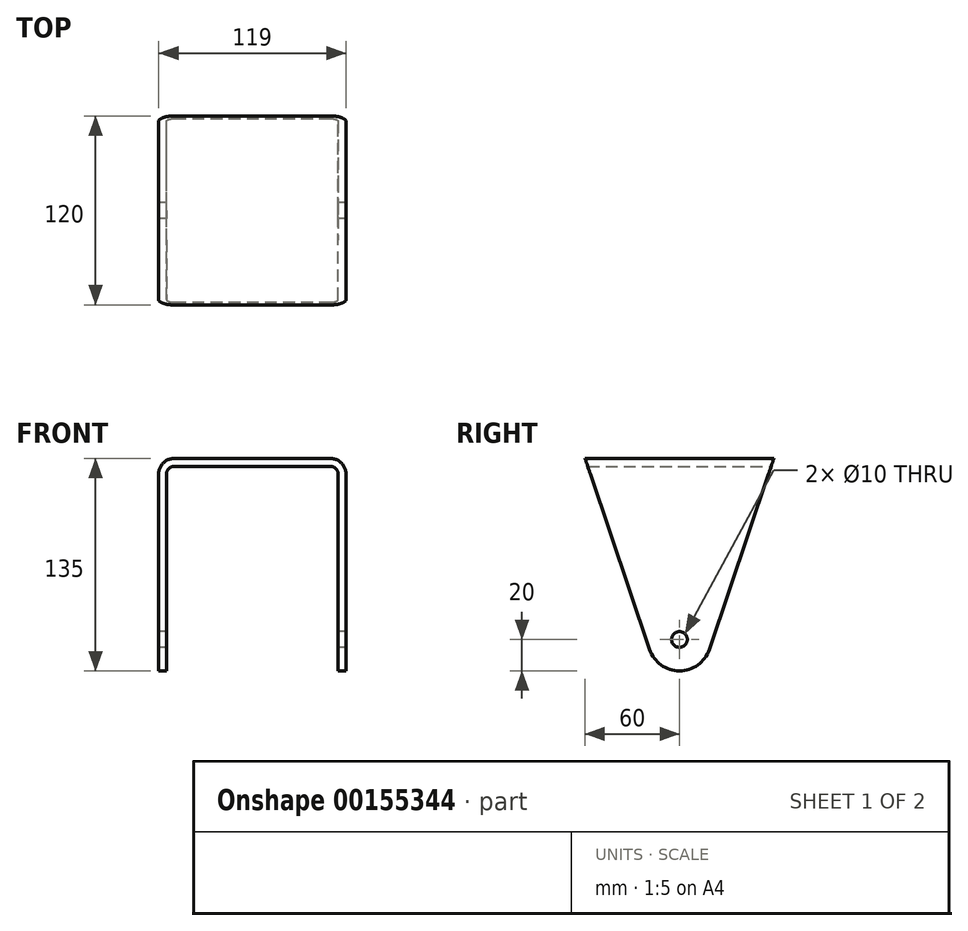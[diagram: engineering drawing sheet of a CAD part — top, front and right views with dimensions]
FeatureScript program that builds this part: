
annotation { "Feature Type Name" : "Feature", "Feature Type Description" : "" }
export const myFeature = defineFeature(function(context is Context, id is Id, definition is map)
    precondition{}
    {
        {
            var Q0;
            Q0=qCreatedBy(makeId("Front.planeOp"),FACE);
            var sketch = newSketch(context, id + "F0", { "sketchPlane" : qUnion([Q0])});
            skLineSegment(sketch, "E0", {"start": v(-29.5, 0) * mm, "end": v(-29.5, -20) * mm});
            skLineSegment(sketch, "E1", {"start": v(-29.5, -20) * mm, "end": v(-34.5, -20) * mm});
            skLineSegment(sketch, "E2", {"start": v(-34.5, -20) * mm, "end": v(-34.5, 105) * mm});
            skLineSegment(sketch, "E3", {"start": v(-24.5, 115) * mm, "end": v(25, 115) * mm});
            skLineSegment(sketch, "E4", {"start": v(-29.5, 0) * mm, "end": v(-29.5, 105) * mm});
            skLineSegment(sketch, "E5.0", {"start": v(-24.5, 110) * mm, "end": v(25, 110) * mm});
            skArc(sketch, "E6.filletArc", {"start": v(-24.5, 110) * mm, "mid": v(-28.04, 108.54) * mm, "end": v(-29.5, 105) * mm});
            skArc(sketch, "E7.0", {"start": v(-24.5, 115) * mm, "mid": v(-31.57, 112.07) * mm, "end": v(-34.5, 105) * mm});
            skLineSegment(sketch, "E8", {"start": v(25, 110) * mm, "end": v(25, 115) * mm});
            skLineSegment(sketch, "E9", {"start": v(25, 128.81) * mm, "end": v(25, 153.22) * mm, "construction": true});
            skArc(sketch, "E10.MirrorCS", {"start": v(74.5, 110) * mm, "mid": v(78.04, 108.54) * mm, "end": v(79.5, 105) * mm});
            skLineSegment(sketch, "E11.MirrorCS", {"start": v(79.5, 0) * mm, "end": v(79.5, 105) * mm});
            skArc(sketch, "E12.MirrorCS", {"start": v(74.5, 115) * mm, "mid": v(81.57, 112.07) * mm, "end": v(84.5, 105) * mm});
            skLineSegment(sketch, "E13.MirrorCS", {"start": v(74.5, 110) * mm, "end": v(25, 110) * mm});
            skLineSegment(sketch, "E14.MirrorCS", {"start": v(74.5, 115) * mm, "end": v(25, 115) * mm});
            skLineSegment(sketch, "E15.MirrorCS", {"start": v(84.5, -20) * mm, "end": v(84.5, 105) * mm});
            skLineSegment(sketch, "E16.MirrorCS", {"start": v(79.5, 0) * mm, "end": v(79.5, -20) * mm});
            skLineSegment(sketch, "E17.MirrorCS", {"start": v(79.5, -20) * mm, "end": v(84.5, -20) * mm});
            skSolve(sketch);
        }
        {
            var Q0;
            Q0=qCreatedBy(makeId("Right.planeOp"),FACE);
            var sketch = newSketch(context, id + "F1", { "sketchPlane" : qUnion([Q0])});
            skArc(sketch, "E18", {"start": v(-18.95, -6.4) * mm, "mid": v(-11.66, -16.25) * mm, "end": v(0, -20) * mm});
            skLineSegment(sketch, "E19", {"start": v(0, 115) * mm, "end": v(-60, 115) * mm});
            skLineSegment(sketch, "E20", {"start": v(0, 0) * mm, "end": v(0, -106.65) * mm, "construction": true});
            skLineSegment(sketch, "E21", {"start": v(-60, 115) * mm, "end": v(-18.95, -6.4) * mm});
            skLineSegment(sketch, "E22", {"start": v(0, 115) * mm, "end": v(0, -20) * mm});
            skLineSegment(sketch, "E23.MirrorCS", {"start": v(0, 115) * mm, "end": v(60, 115) * mm});
            skLineSegment(sketch, "E24.MirrorCS", {"start": v(60, 115) * mm, "end": v(18.95, -6.4) * mm});
            skArc(sketch, "E25.MirrorCS", {"start": v(18.95, -6.4) * mm, "mid": v(11.66, -16.25) * mm, "end": v(0, -20) * mm});
            skCircle(sketch, "E26", {"center": v(0, 0) * mm, "radius": 5 * mm});
            skSolve(sketch);
        }
        {
            var Q0;
            Q0=makeQuery(id+"F0.imprint","IMPRINT",FACE,{"disambiguationData":[TD([[makeQuery(id+"F0.imprint","IMPRINT",EDGE,{"derivedFrom":sQuery(id+"F0.wireOp",EDGE,"E8")}),-1.0]])]});
            var Q1;
            Q1=makeQuery(id+"F0.imprint","IMPRINT",FACE,{"disambiguationData":[TD([[makeQuery(id+"F0.imprint","IMPRINT",EDGE,{"derivedFrom":sQuery(id+"F0.wireOp",EDGE,"E0")}),-1.0]])]});
            extrude(context, id + "F2", {"entities" : qUnion([Q0, Q1]), "depth" : 80 * mm, "hasSecondDirection" : true, "secondDirectionOppositeDirection" : true, "secondDirectionDepth" : 80 * mm});
        }
        {
            var Q0;
            Q0=makeQuery(id+"F1.imprint","IMPRINT",FACE,{"disambiguationData":[TD([[makeQuery(id+"F1.imprint","IMPRINT",EDGE,{"derivedFrom":sQuery(id+"F1.wireOp",EDGE,"E18")}),1.0]])]});
            var Q1;
            Q1=makeQuery(id+"F1.imprint","IMPRINT",FACE,{"disambiguationData":[TD([[makeQuery(id+"F1.imprint","IMPRINT",EDGE,{"derivedFrom":sQuery(id+"F1.wireOp",EDGE,"E22")}),1.0]])]});
            extrude(context, id + "F3", {"entities" : qUnion([Q0, Q1]), "operationType" : NewBodyOperationType.INTERSECT, "endBound" : BoundingType.THROUGH_ALL, "depth" : 98.75 * mm, "hasSecondDirection" : true, "secondDirectionBound" : SecondDirectionBoundingType.THROUGH_ALL, "secondDirectionOppositeDirection" : true, "secondDirectionDepth" : 25 * mm});
        }
    });
